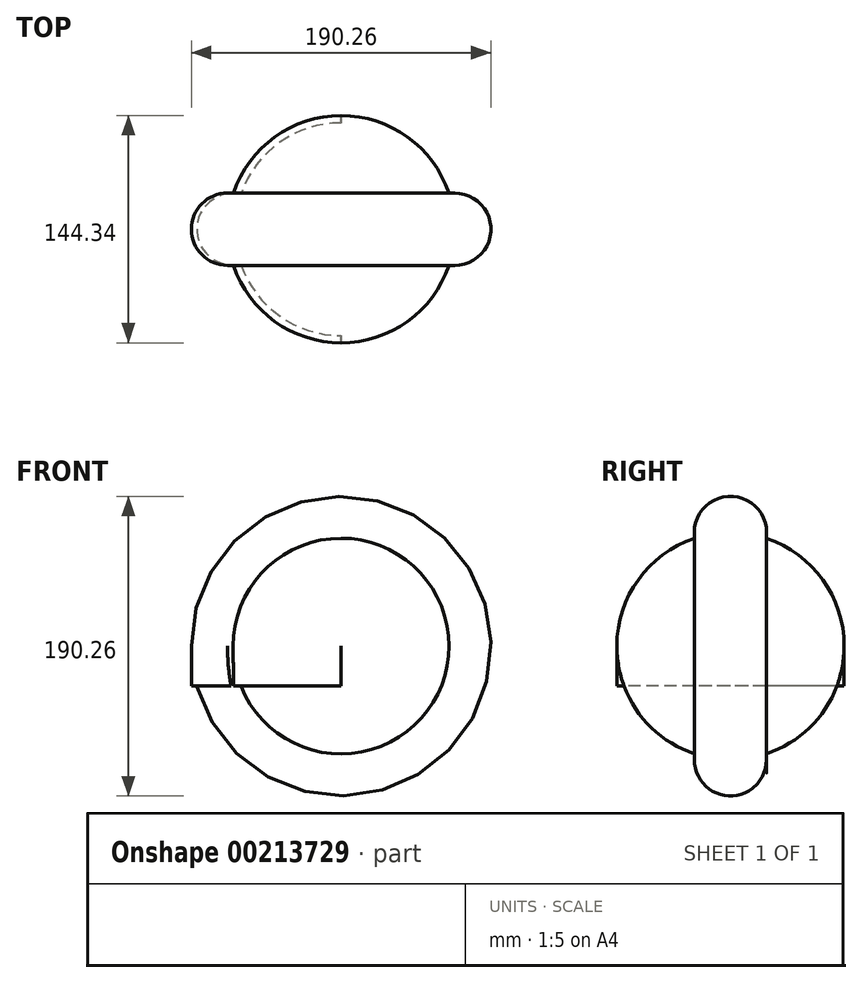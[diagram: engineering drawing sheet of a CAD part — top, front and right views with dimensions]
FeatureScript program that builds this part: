
annotation { "Feature Type Name" : "Feature", "Feature Type Description" : "" }
export const myFeature = defineFeature(function(context is Context, id is Id, definition is map)
    precondition{}
    {
        {
            var Q0;
            Q0=qCreatedBy(makeId("Top.planeOp"),FACE);
            var sketch = newSketch(context, id + "F0", { "sketchPlane" : qUnion([Q0])});
            skArc(sketch, "E0", {"start": v(-68.52, -22.67) * mm, "mid": v(-42.27, -58.5) * mm, "end": v(0, -72.17) * mm});
            skLineSegment(sketch, "E1", {"start": v(0, 72.17) * mm, "end": v(0, -72.17) * mm});
            skArc(sketch, "E2", {"start": v(-68.52, 22.67) * mm, "mid": v(-95.13, 0) * mm, "end": v(-68.52, -22.67) * mm});
            skArc(sketch, "E3.trimOffspring", {"start": v(0, 72.17) * mm, "mid": v(-42.27, 58.5) * mm, "end": v(-68.52, 22.67) * mm});
            skSolve(sketch);
        }
        {
            var Q0;
            Q0=makeQuery(id+"F0.imprint","IMPRINT",FACE,{"disambiguationData":[TD([[makeQuery(id+"F0.imprint","IMPRINT",EDGE,{"derivedFrom":sQuery(id+"F0.wireOp",EDGE,"E0")}),1.0]])]});
            extrude(context, id + "F1", {"entities" : qUnion([Q0]), "depth" : 25.4 * mm});
        }
        {
            var Q0;
            Q0=makeQuery(id+"F1.opExtrude","CAP_FACE",FACE,{"disambiguationData":[OSD([sQuery(id+"F0.wireOp",EDGE,"E0"),sQuery(id+"F0.wireOp",EDGE,"E2"),sQuery(id+"F0.wireOp",EDGE,"E3.trimOffspring"),sQuery(id+"F0.wireOp",EDGE,"E1")])],"isStart":false});
            var Q1;
            Q1=makeQuery(id+"F1.opExtrude","CAP_EDGE",EDGE,{"disambiguationData":[OSD([sQuery(id+"F0.wireOp",EDGE,"E1")])],"isStart":false});
            revolve(context, id + "F2", {"operationType" : NewBodyOperationType.ADD, "entities" : qUnion([Q0]), "axis" : qUnion([Q1]), "revolveType" : RevolveType.FULL});
        }
    });
